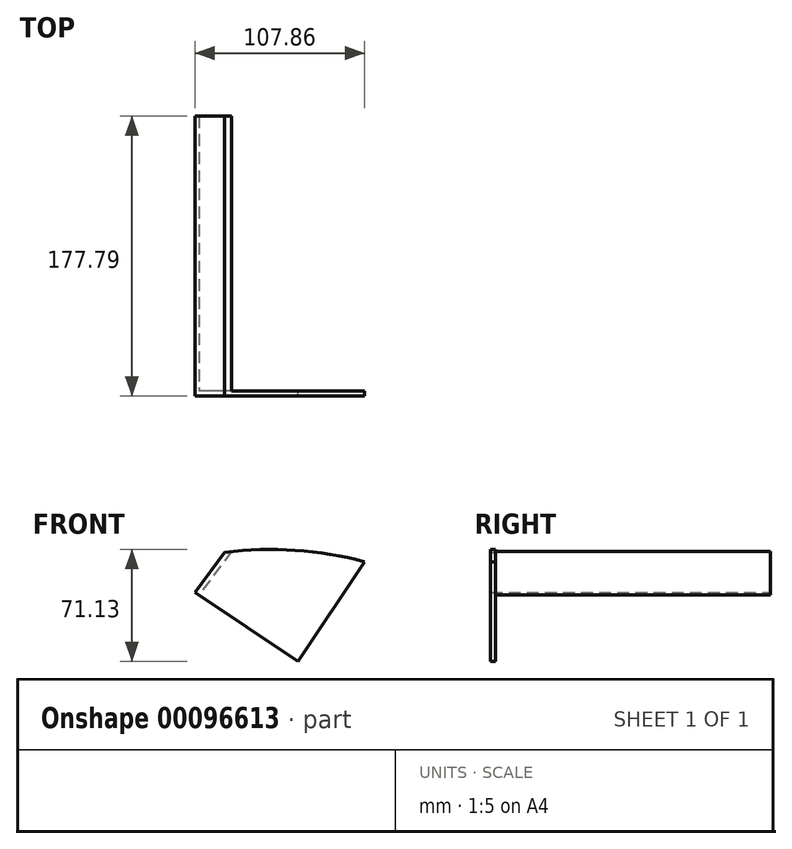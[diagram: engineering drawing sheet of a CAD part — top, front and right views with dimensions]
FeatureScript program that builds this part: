
annotation { "Feature Type Name" : "Feature", "Feature Type Description" : "" }
export const myFeature = defineFeature(function(context is Context, id is Id, definition is map)
    precondition{}
    {
        {
            var Q0;
            Q0=qCreatedBy(makeId("Front.planeOp"),FACE);
            var sketch = newSketch(context, id + "F0", { "sketchPlane" : qUnion([Q0])});
            skCircle(sketch, "E0", {"center": v(0, 0) * mm, "radius": 228.6 * mm});
            skLineSegment(sketch, "E1", {"start": v(59.4, 220.75) * mm, "end": v(20.5, 162.74) * mm});
            skLineSegment(sketch, "E2", {"start": v(11.68, 161) * mm, "end": v(-42.9, 197.62) * mm});
            skLineSegment(sketch, "E3", {"start": v(-44.45, 206.7) * mm, "end": v(-29.47, 226.7) * mm});
            skPoint(sketch, "E4.visualSharp", {"position": v(-48.46, 201.35) * mm});
            skPoint(sketch, "E5.visualSharp", {"position": v(16.95, 157.47) * mm});
            skLineSegment(sketch, "E6", {"start": v(-44.45, 206.7) * mm, "end": v(-48.46, 201.35) * mm});
            skLineSegment(sketch, "E7", {"start": v(-42.9, 197.62) * mm, "end": v(-48.46, 201.35) * mm});
            skLineSegment(sketch, "E8", {"start": v(20.5, 162.74) * mm, "end": v(16.95, 157.47) * mm});
            skLineSegment(sketch, "E9", {"start": v(11.68, 161) * mm, "end": v(16.95, 157.47) * mm});
            skSolve(sketch);
        }
        {
            var Q0;
            {var subQ1=sQuery(id+"F0.wireOp",EDGE,"E1");Q0=makeQuery(id+"F0.imprint","IMPRINT",FACE,{"disambiguationData":[TD([[makeQuery(id+"F0.imprint","IMPRINT",EDGE,{"derivedFrom":subQ1}),-1.0]])]});}
            extrude(context, id + "F1", {"entities" : qUnion([Q0]), "depth" : 3.17 * mm});
        }
        {
            var Q0;
            Q0=makeQuery(id+"F1.opExtrude","CAP_FACE",FACE,{"disambiguationData":[OSD([sQuery(id+"F0.wireOp",EDGE,"E0"),sQuery(id+"F0.wireOp",EDGE,"E1"),sQuery(id+"F0.wireOp",EDGE,"E2"),sQuery(id+"F0.wireOp",EDGE,"E3"),sQuery(id+"F0.wireOp",EDGE,"E6"),sQuery(id+"F0.wireOp",EDGE,"E7"),sQuery(id+"F0.wireOp",EDGE,"E8"),sQuery(id+"F0.wireOp",EDGE,"E9")])],"isStart":true});
            var sketch = newSketch(context, id + "F2", { "sketchPlane" : qUnion([Q0])});
            skLineSegment(sketch, "E10", {"start": v(29.47, 226.7) * mm, "end": v(48.46, 201.35) * mm});
            skLineSegment(sketch, "E11", {"start": v(48.46, 201.35) * mm, "end": v(-16.95, 157.47) * mm});
            skLineSegment(sketch, "E12", {"start": v(-16.95, 157.47) * mm, "end": v(-59.4, 220.75) * mm});
            skLineSegment(sketch, "E13", {"start": v(-59.4, 220.75) * mm, "end": v(-16.95, 157.47) * mm});
            skArc(sketch, "E14", {"start": v(29.47, 226.7) * mm, "mid": v(-15.26, 228.08) * mm, "end": v(-59.4, 220.75) * mm});
            skLineSegment(sketch, "E15", {"start": v(29.47, 226.7) * mm, "end": v(26.96, 224.81) * mm});
            skLineSegment(sketch, "E16", {"start": v(26.96, 224.81) * mm, "end": v(45.86, 199.6) * mm});
            skLineSegment(sketch, "E17", {"start": v(45.86, 199.6) * mm, "end": v(25.16, 227.2) * mm});
            skLineSegment(sketch, "E18", {"start": v(25.16, 227.2) * mm, "end": v(45.86, 199.6) * mm});
            skLineSegment(sketch, "E19", {"start": v(-16.95, 157.47) * mm, "end": v(-14.5, 159.12) * mm});
            skLineSegment(sketch, "E20", {"start": v(-14.5, 159.12) * mm, "end": v(-56.37, 221.54) * mm});
            skLineSegment(sketch, "E21", {"start": v(-56.37, 221.54) * mm, "end": v(-14.5, 159.12) * mm});
            skLineSegment(sketch, "E22", {"start": v(-16.95, 157.47) * mm, "end": v(-18.75, 160.15) * mm});
            skLineSegment(sketch, "E23", {"start": v(-18.75, 160.15) * mm, "end": v(46.52, 203.93) * mm});
            skLineSegment(sketch, "E24", {"start": v(46.52, 203.93) * mm, "end": v(-18.75, 160.15) * mm});
            skSolve(sketch);
        }
        {
            var Q0;
            {var subQ1=sQuery(id+"F2.wireOp",EDGE,"E11");var subQ3=sQuery(id+"F2.wireOp",EDGE,"E18");var subQ4=makeQuery(id+"F2.imprint","INTERSECT",VERTEX,{"derivedFrom":[subQ1,subQ3]});Q0=makeQuery(id+"F2.imprint","IMPRINT",FACE,{"disambiguationData":[TD([[makeQuery(id+"F2.imprint","IMPRINT",EDGE,{"disambiguationData":[TD([[subQ4,1.0]])],"derivedFrom":subQ3}),-1.0]])]});}
            var Q1;
            {var subQ0=sQuery(id+"F2.wireOp",EDGE,"E19");Q1=makeQuery(id+"F2.imprint","IMPRINT",FACE,{"disambiguationData":[TD([[makeQuery(id+"F2.imprint","IMPRINT",EDGE,{"derivedFrom":subQ0}),1.0]])]});}
            var Q2;
            {var subQ0=sQuery(id+"F2.wireOp",EDGE,"E13");Q2=makeQuery(id+"F2.imprint","IMPRINT",FACE,{"disambiguationData":[TD([[makeQuery(id+"F2.imprint","IMPRINT",EDGE,{"derivedFrom":subQ0}),1.0]])]});}
            var Q3;
            {var subQ0=sQuery(id+"F2.wireOp",EDGE,"E11");var subQ1=sQuery(id+"F2.wireOp",EDGE,"E10");var subQ2=makeQuery(id+"F2.imprint","INTERSECT",VERTEX,{"derivedFrom":[subQ1,subQ0]});Q3=makeQuery(id+"F2.imprint","IMPRINT",FACE,{"disambiguationData":[TD([[makeQuery(id+"F2.imprint","IMPRINT",EDGE,{"disambiguationData":[TD([[subQ2,-1.0]])],"derivedFrom":subQ1}),1.0]])]});}
            var Q4;
            {var subQ0=sQuery(id+"F2.wireOp",EDGE,"E15");Q4=makeQuery(id+"F2.imprint","IMPRINT",FACE,{"disambiguationData":[TD([[makeQuery(id+"F2.imprint","IMPRINT",EDGE,{"derivedFrom":subQ0}),1.0]])]});}
            var Q5;
            {var subQ0=sQuery(id+"F2.wireOp",EDGE,"E15");Q5=makeQuery(id+"F2.imprint","IMPRINT",FACE,{"disambiguationData":[TD([[makeQuery(id+"F2.imprint","IMPRINT",EDGE,{"derivedFrom":subQ0}),-1.0]])]});}
            extrude(context, id + "F3", {"entities" : qUnion([Q0, Q1, Q2, Q3, Q4, Q5]), "operationType" : NewBodyOperationType.ADD, "depth" : 174.62 * mm});
        }
    });
